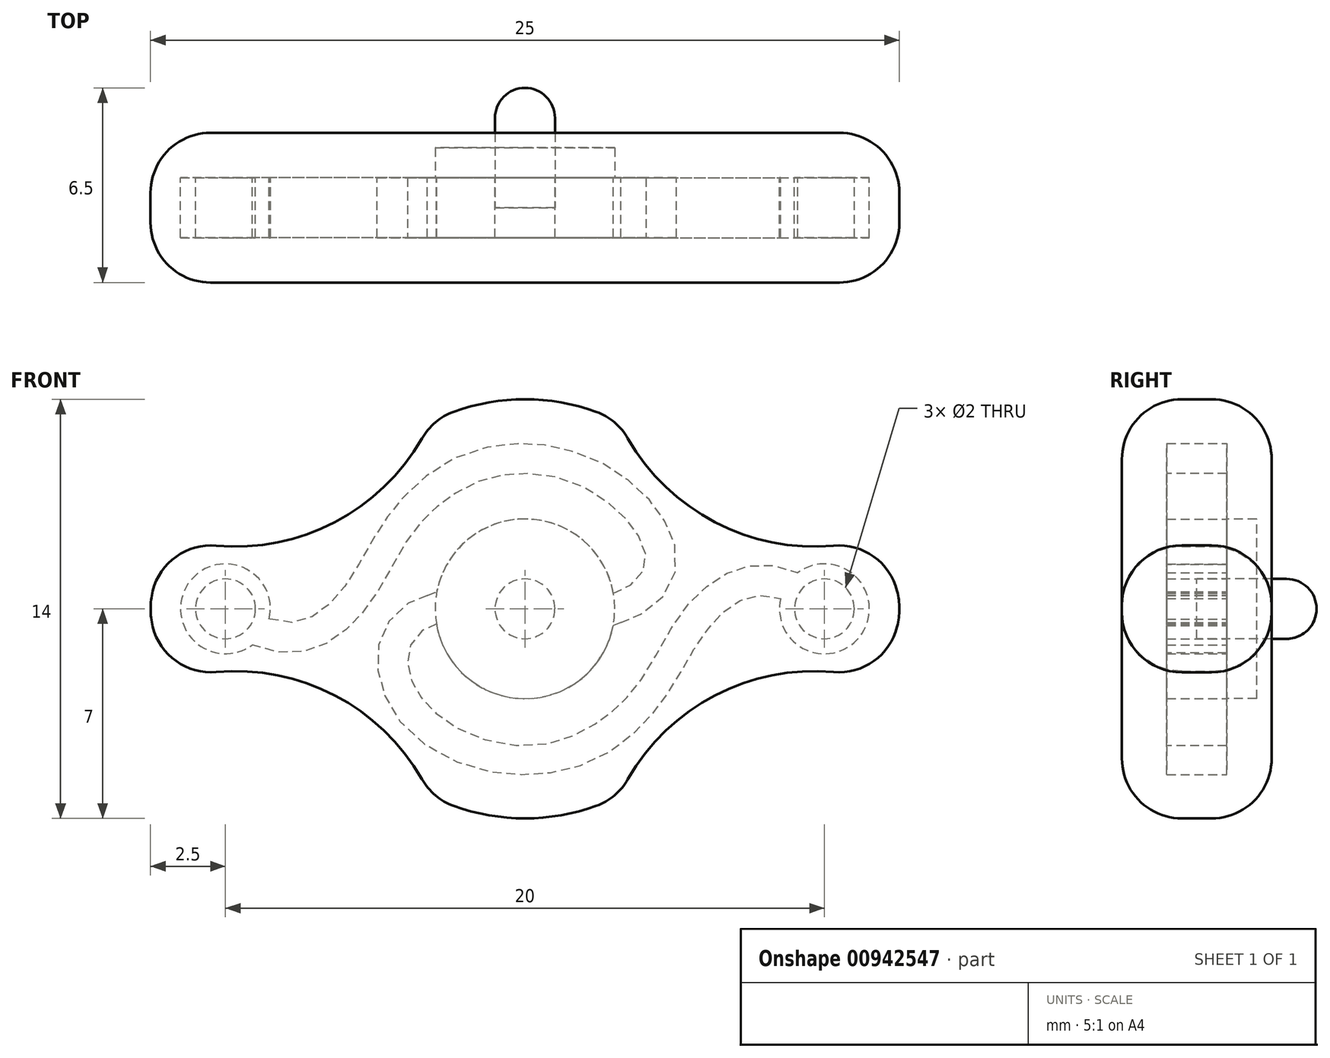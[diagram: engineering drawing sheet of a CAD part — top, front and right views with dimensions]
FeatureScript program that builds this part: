
annotation { "Feature Type Name" : "Feature", "Feature Type Description" : "" }
export const myFeature = defineFeature(function(context is Context, id is Id, definition is map)
    precondition{}
    {
        {
            var Q0;
            Q0=qCreatedBy(makeId("Front.planeOp"),FACE);
            var sketch = newSketch(context, id + "F0", { "sketchPlane" : qUnion([Q0])});
            skCircle(sketch, "E0", {"center": v(0, 0) * mm, "radius": 3 * mm});
            skFitSpline(sketch, "E1.0", {"points": [v(3.18, -0.47) * mm, v(3.53, -0.33) * mm, v(4.14, -0.02) * mm, v(4.75, 0.6) * mm, v(5.04, 1.35) * mm, v(5, 2.1) * mm, v(4.75, 2.78) * mm, v(4.36, 3.38) * mm, v(3.87, 3.93) * mm, v(3.1, 4.56) * mm, v(2.18, 5.05) * mm, v(1.2, 5.36) * mm, v(0.44, 5.5) * mm, v(-0.32, 5.51) * mm, v(-1.3, 5.39) * mm, v(-2.46, 4.98) * mm, v(-3.45, 4.3) * mm, v(-4.13, 3.66) * mm, v(-4.56, 3.12) * mm, v(-4.92, 2.57) * mm, v(-5.35, 1.84) * mm, v(-5.74, 1.15) * mm, v(-6.17, 0.55) * mm, v(-6.53, 0.16) * mm, v(-6.92, -0.16) * mm, v(-7.34, -0.36) * mm, v(-7.8, -0.45) * mm, v(-8.31, -0.4) * mm, v(-8.93, -0.16) * mm, v(-9.42, 0.17) * mm, v(-9.68, 0.38) * mm]});
            skFitSpline(sketch, "E2.0", {"points": [v(2.82, 0.47) * mm, v(3.11, 0.58) * mm, v(3.56, 0.82) * mm, v(3.9, 1.18) * mm, v(4.02, 1.5) * mm, v(4.02, 1.88) * mm, v(3.86, 2.31) * mm, v(3.57, 2.77) * mm, v(3.18, 3.2) * mm, v(2.55, 3.72) * mm, v(1.6, 4.23) * mm, v(0.54, 4.49) * mm, v(-0.27, 4.51) * mm, v(-1.06, 4.41) * mm, v(-1.81, 4.14) * mm, v(-2.5, 3.74) * mm, v(-2.97, 3.38) * mm, v(-3.39, 2.98) * mm, v(-3.86, 2.39) * mm, v(-4.37, 1.54) * mm, v(-4.88, 0.63) * mm, v(-5.38, -0.07) * mm, v(-5.83, -0.56) * mm, v(-6.37, -1) * mm, v(-7, -1.32) * mm, v(-7.75, -1.47) * mm, v(-8.57, -1.38) * mm, v(-9.42, -1.04) * mm, v(-10.02, -0.64) * mm, v(-10.32, -0.38) * mm]});
            skCircle(sketch, "E3", {"center": v(-10, 0) * mm, "radius": 1.5 * mm});
            skLineSegment(sketch, "E4", {"start": v(3.27, -0.43) * mm, "end": v(2.95, -0.56) * mm});
            skFitSpline(sketch, "E5.0", {"points": [v(-3.15, 0.48) * mm, v(-3.46, 0.38) * mm, v(-4.01, 0.11) * mm, v(-4.59, -0.49) * mm, v(-4.88, -1.21) * mm, v(-4.92, -1.96) * mm, v(-4.75, -2.7) * mm, v(-4.3, -3.59) * mm, v(-3.4, -4.49) * mm, v(-2, -5.21) * mm, v(-0.7, -5.5) * mm, v(0.32, -5.52) * mm, v(1.32, -5.39) * mm, v(2.47, -4.98) * mm, v(3.45, -4.31) * mm, v(4.12, -3.67) * mm, v(4.55, -3.14) * mm, v(4.91, -2.6) * mm, v(5.35, -1.88) * mm, v(5.74, -1.19) * mm, v(6.18, -0.59) * mm, v(6.54, -0.19) * mm, v(6.94, 0.14) * mm, v(7.37, 0.36) * mm, v(7.82, 0.45) * mm, v(8.33, 0.4) * mm, v(8.94, 0.17) * mm, v(9.42, -0.16) * mm, v(9.68, -0.38) * mm]});
            skFitSpline(sketch, "E6.0", {"points": [v(-2.85, -0.48) * mm, v(-3.08, -0.55) * mm, v(-3.43, -0.73) * mm, v(-3.73, -1.05) * mm, v(-3.89, -1.42) * mm, v(-3.91, -1.86) * mm, v(-3.8, -2.34) * mm, v(-3.57, -2.81) * mm, v(-3.22, -3.24) * mm, v(-2.62, -3.76) * mm, v(-1.65, -4.26) * mm, v(-0.35, -4.56) * mm, v(0.88, -4.48) * mm, v(1.82, -4.14) * mm, v(2.5, -3.74) * mm, v(2.96, -3.39) * mm, v(3.38, -2.99) * mm, v(3.86, -2.4) * mm, v(4.37, -1.56) * mm, v(5, -0.48) * mm, v(5.66, 0.39) * mm, v(6.38, 0.98) * mm, v(7.02, 1.3) * mm, v(7.76, 1.47) * mm, v(8.58, 1.4) * mm, v(9.44, 1.05) * mm, v(10.02, 0.64) * mm, v(10.32, 0.38) * mm]});
            skLineSegment(sketch, "E7", {"start": v(-3.41, 0.38) * mm, "end": v(-2.94, 0.57) * mm});
            skCircle(sketch, "E8", {"center": v(10, 0) * mm, "radius": 1.5 * mm});
            skCircle(sketch, "E9", {"center": v(0, 0) * mm, "radius": 1 * mm});
            skCircle(sketch, "E10", {"center": v(-10, 0) * mm, "radius": 1 * mm});
            skCircle(sketch, "E11", {"center": v(10, 0) * mm, "radius": 1 * mm});
            skSolve(sketch);
        }
        {
            var Q0;
            Q0 = qSketchRegion(id + "F0", true);
            extrude(context, id + "F1", {"entities" : qUnion([Q0]), "endBound" : BoundingType.SYMMETRIC, "depth" : 2 * mm, "offsetDistance" : 25 * mm});
        }
        {
            var Q0;
            Q0=makeQuery(id+"F1.opExtrude","CAP_FACE",FACE,{"disambiguationData":[OSD([sQuery(id+"F0.wireOp",EDGE,"E0"),sQuery(id+"F0.wireOp",EDGE,"E1.0"),sQuery(id+"F0.wireOp",EDGE,"E2.0"),sQuery(id+"F0.wireOp",EDGE,"E3"),sQuery(id+"F0.wireOp",EDGE,"E4"),sQuery(id+"F0.wireOp",EDGE,"E5.0"),sQuery(id+"F0.wireOp",EDGE,"E6.0"),sQuery(id+"F0.wireOp",EDGE,"E7"),sQuery(id+"F0.wireOp",EDGE,"E8"),sQuery(id+"F0.wireOp",EDGE,"E9"),sQuery(id+"F0.wireOp",EDGE,"E10"),sQuery(id+"F0.wireOp",EDGE,"E11")])],"isStart":true});
            var sketch = newSketch(context, id + "F2", { "sketchPlane" : qUnion([Q0])});
            skCircle(sketch, "E12", {"center": v(0, 0) * mm, "radius": 3 * mm});
            skSolve(sketch);
        }
        {
            var Q0;
            Q0=qCreatedBy(makeId("Front.planeOp"),FACE);
            var sketch = newSketch(context, id + "F3", { "sketchPlane" : qUnion([Q0])});
            skCircle(sketch, "E13", {"center": v(0, 0) * mm, "radius": 1 * mm});
            skSolve(sketch);
        }
        {
            var Q0;
            Q0 = qSketchRegion(id + "F2", true);
            extrude(context, id + "F4", {"entities" : qUnion([Q0]), "depth" : 1 * mm, "offsetDistance" : 25 * mm});
        }
        {
            var Q0;
            Q0 = qSketchRegion(id + "F3", true);
            extrude(context, id + "F5", {"entities" : qUnion([Q0]), "oppositeDirection" : true, "depth" : 4 * mm, "offsetDistance" : 25 * mm});
        }
        {
            var Q0;
            Q0=qCreatedBy(makeId("Front.planeOp"),FACE);
            var sketch = newSketch(context, id + "F6", { "sketchPlane" : qUnion([Q0])});
            skArc(sketch, "E14", {"start": v(12.43, -0.6) * mm, "mid": v(12.5, 0) * mm, "end": v(12.43, 0.6) * mm});
            skArc(sketch, "E15", {"start": v(-12.43, 0.6) * mm, "mid": v(-12.5, 0) * mm, "end": v(-12.43, -0.6) * mm});
            skArc(sketch, "E16", {"start": v(-2.38, -6.58) * mm, "mid": v(0, -7) * mm, "end": v(2.38, -6.58) * mm});
            skArc(sketch, "E17.trimOffspring", {"start": v(2.38, 6.58) * mm, "mid": v(0, 7) * mm, "end": v(-2.38, 6.58) * mm});
            skArc(sketch, "E18", {"start": v(-10.3, 2.11) * mm, "mid": v(-6.35, 2.9) * mm, "end": v(-3.44, 5.7) * mm});
            skPoint(sketch, "E19.visualSharp", {"position": v(-11.12, 2.23) * mm});
            skArc(sketch, "E19.filletArc", {"start": v(-10.3, 2.11) * mm, "mid": v(-11.65, 1.75) * mm, "end": v(-12.43, 0.6) * mm});
            skPoint(sketch, "E20.visualSharp", {"position": v(-3.15, 6.25) * mm});
            skArc(sketch, "E20.filletArc", {"start": v(-2.38, 6.58) * mm, "mid": v(-2.99, 6.23) * mm, "end": v(-3.44, 5.7) * mm});
            skArc(sketch, "E21.MirrorCS", {"start": v(10.3, 2.11) * mm, "mid": v(6.35, 2.9) * mm, "end": v(3.44, 5.7) * mm});
            skArc(sketch, "E22.MirrorCS", {"start": v(-10.3, -2.11) * mm, "mid": v(-6.35, -2.9) * mm, "end": v(-3.44, -5.7) * mm});
            skArc(sketch, "E23.MirrorCS", {"start": v(10.3, -2.11) * mm, "mid": v(6.35, -2.9) * mm, "end": v(3.44, -5.7) * mm});
            skPoint(sketch, "E24.newPointA", {"position": v(-3.44, -5.7) * mm});
            skArc(sketch, "E24.filletArc", {"start": v(-3.44, -5.7) * mm, "mid": v(-2.99, -6.23) * mm, "end": v(-2.38, -6.58) * mm});
            skPoint(sketch, "E25.newPointB", {"position": v(-10.3, -2.11) * mm});
            skArc(sketch, "E25.filletArc", {"start": v(-12.43, -0.6) * mm, "mid": v(-11.65, -1.75) * mm, "end": v(-10.3, -2.11) * mm});
            skPoint(sketch, "E26.newPointB", {"position": v(3.44, -5.7) * mm});
            skArc(sketch, "E26.filletArc", {"start": v(2.38, -6.58) * mm, "mid": v(2.99, -6.23) * mm, "end": v(3.44, -5.7) * mm});
            skPoint(sketch, "E27.newPointA", {"position": v(10.3, -2.11) * mm});
            skArc(sketch, "E27.filletArc", {"start": v(10.3, -2.11) * mm, "mid": v(11.65, -1.75) * mm, "end": v(12.43, -0.6) * mm});
            skPoint(sketch, "E28.newPointA", {"position": v(10.3, 2.11) * mm});
            skArc(sketch, "E28.filletArc", {"start": v(12.43, 0.6) * mm, "mid": v(11.65, 1.75) * mm, "end": v(10.3, 2.11) * mm});
            skPoint(sketch, "E29.newPointB", {"position": v(3.44, 5.7) * mm});
            skArc(sketch, "E29.filletArc", {"start": v(3.44, 5.7) * mm, "mid": v(2.99, 6.23) * mm, "end": v(2.38, 6.58) * mm});
            skSolve(sketch);
        }
        {
            var Q0;
            Q0 = qSketchRegion(id + "F6", true);
            extrude(context, id + "F7", {"entities" : qUnion([Q0]), "endBound" : BoundingType.SYMMETRIC, "depth" : 5 * mm, "offsetDistance" : 25 * mm});
        }
        {
            var Q0;
            Q0=makeQuery(id+"F7.opExtrude","CAP_EDGE",EDGE,{"disambiguationData":[OSD([sQuery(id+"F6.wireOp",EDGE,"E18")])],"isStart":false});
            var Q1;
            Q1=makeQuery(id+"F7.opExtrude","CAP_EDGE",EDGE,{"disambiguationData":[OSD([sQuery(id+"F6.wireOp",EDGE,"E22.MirrorCS")])],"isStart":true});
            fillet(context, id + "F8", {"entities" : qUnion([Q0, Q1]), "radius" : 2 * mm, "tangentPropagation" : true, "allowEdgeOverflow" : false});
        }
        {
            var Q0;
            Q0=makeQuery(id+"F5.opExtrude","CAP_FACE",FACE,{"disambiguationData":[OSD([sQuery(id+"F3.wireOp",EDGE,"E13")])],"isStart":false});
            fillet(context, id + "F9", {"entities" : qUnion([Q0]), "radius" : 1 * mm, "tangentPropagation" : true, "allowEdgeOverflow" : false});
        }
    });
